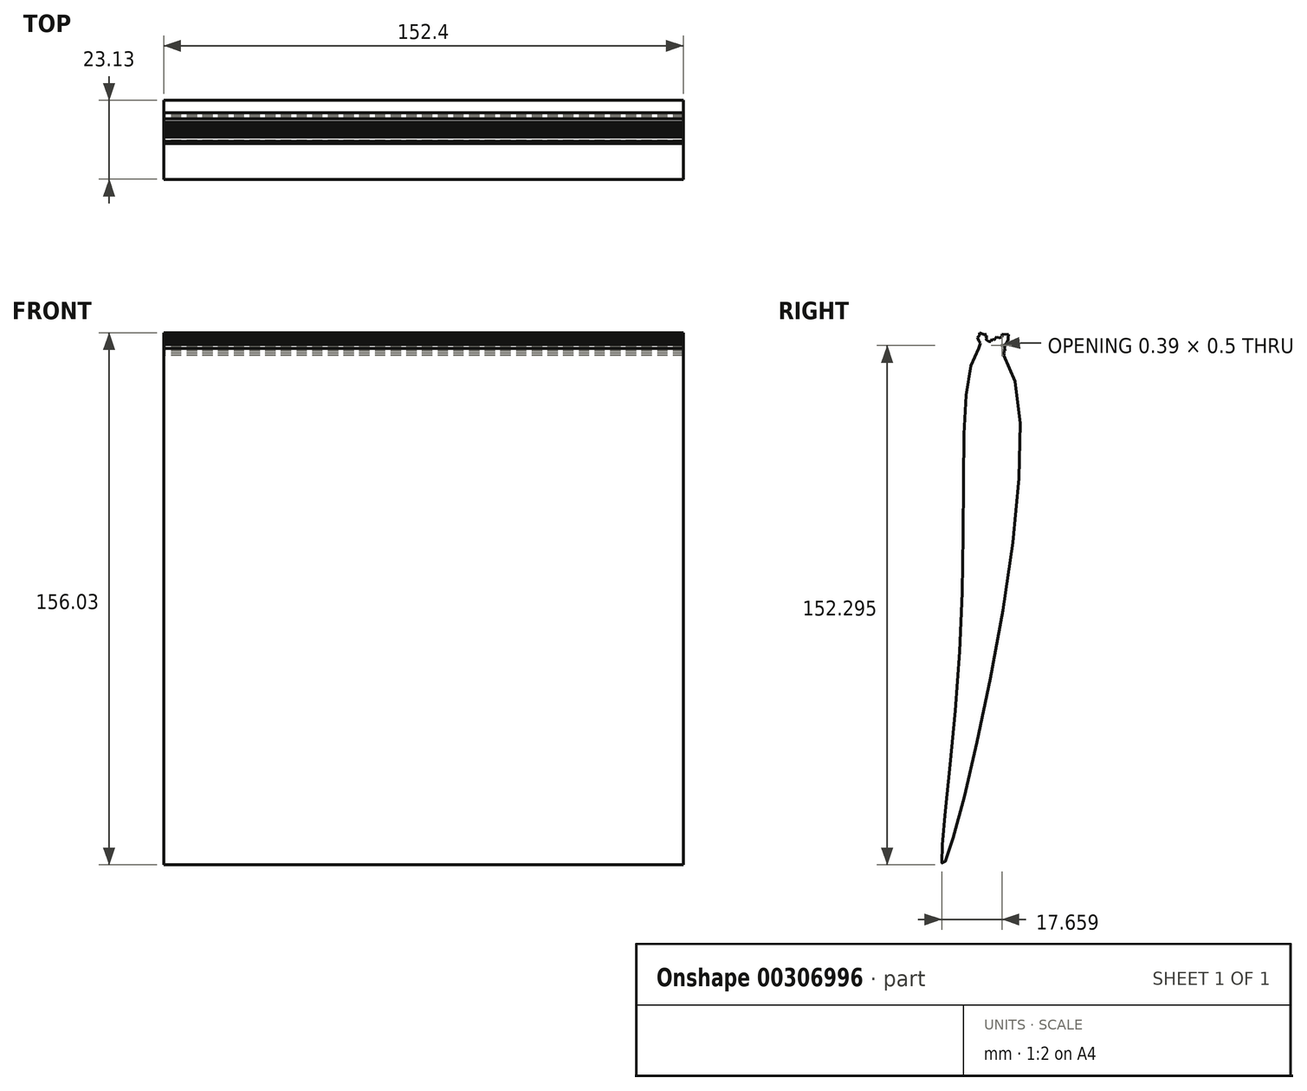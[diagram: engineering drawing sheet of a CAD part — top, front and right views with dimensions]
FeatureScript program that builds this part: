
annotation { "Feature Type Name" : "Feature", "Feature Type Description" : "" }
export const myFeature = defineFeature(function(context is Context, id is Id, definition is map)
    precondition{}
    {
        {
            var Q0;
            Q0=qCreatedBy(makeId("Right.planeOp"),FACE);
            var sketch = newSketch(context, id + "F0", { "sketchPlane" : qUnion([Q0])});
            skFitSpline(sketch, "E0", {"points": [v(8.56, 74.97) * mm, v(19.4, 61.14) * mm, v(-2.03, -76.46) * mm, v(2.7, -8.93) * mm, v(8.56, 74.97) * mm]});
            skLineSegment(sketch, "E1", {"start": v(12.68, 75.05) * mm, "end": v(15.09, 77.75) * mm});
            skLineSegment(sketch, "E2", {"start": v(15.09, 77.75) * mm, "end": v(16.1, 76.96) * mm});
            skLineSegment(sketch, "E3", {"start": v(16.1, 76.96) * mm, "end": v(13.9, 74.13) * mm});
            skLineSegment(sketch, "E4", {"start": v(13.9, 74.13) * mm, "end": v(12.68, 75.05) * mm});
            skLineSegment(sketch, "E5", {"start": v(15.09, 77.75) * mm, "end": v(15.68, 78.5) * mm});
            skPoint(sketch, "E5.endSnap0", {"position": v(15.6, 77.36) * mm});
            skLineSegment(sketch, "E6", {"start": v(15.68, 78.5) * mm, "end": v(16.65, 77.64) * mm});
            skLineSegment(sketch, "E7", {"start": v(16.65, 77.64) * mm, "end": v(16.1, 76.96) * mm});
            skLineSegment(sketch, "E8", {"start": v(10.23, 75.65) * mm, "end": v(9.38, 78.15) * mm});
            skLineSegment(sketch, "E9", {"start": v(9.38, 78.15) * mm, "end": v(8.15, 77.73) * mm});
            skLineSegment(sketch, "E10", {"start": v(8.15, 77.73) * mm, "end": v(9, 75.25) * mm});
            skLineSegment(sketch, "E11", {"start": v(9, 75.25) * mm, "end": v(10.23, 75.65) * mm});
            skLineSegment(sketch, "E12", {"start": v(14.51, 73.62) * mm, "end": v(14.61, 75.05) * mm});
            skLineSegment(sketch, "E13", {"start": v(14.61, 75.05) * mm, "end": v(15, 75.55) * mm});
            skLineSegment(sketch, "E14", {"start": v(15, 75.55) * mm, "end": v(14.99, 75.28) * mm});
            skPoint(sketch, "E14.endSnap0", {"position": v(14.8, 75.3) * mm});
            skLineSegment(sketch, "E15", {"start": v(14.99, 75.28) * mm, "end": v(14.61, 75.05) * mm});
            skLineSegment(sketch, "E16", {"start": v(14.56, 74.33) * mm, "end": v(15.2, 75.14) * mm});
            skLineSegment(sketch, "E17", {"start": v(15.2, 75.14) * mm, "end": v(15.24, 75.85) * mm});
            skLineSegment(sketch, "E18", {"start": v(15.24, 75.85) * mm, "end": v(15.69, 75.5) * mm});
            skLineSegment(sketch, "E19", {"start": v(15.69, 75.5) * mm, "end": v(15.2, 75.14) * mm});
            skLineSegment(sketch, "E20", {"start": v(15.8, 76.57) * mm, "end": v(16.65, 76.5) * mm});
            skLineSegment(sketch, "E21", {"start": v(16.65, 76.5) * mm, "end": v(16.1, 76.96) * mm});
            skLineSegment(sketch, "E22", {"start": v(16.65, 77.64) * mm, "end": v(16.68, 76.92) * mm});
            skLineSegment(sketch, "E23", {"start": v(16.68, 76.92) * mm, "end": v(16.05, 76.11) * mm});
            skLineSegment(sketch, "E24", {"start": v(16.05, 76.11) * mm, "end": v(15.24, 75.85) * mm});
            skLineSegment(sketch, "E25", {"start": v(16.05, 76.11) * mm, "end": v(16.03, 75.8) * mm});
            skLineSegment(sketch, "E26", {"start": v(16.03, 75.8) * mm, "end": v(15.69, 75.5) * mm});
            skLineSegment(sketch, "E27", {"start": v(16.68, 76.92) * mm, "end": v(16.1, 76.96) * mm});
            skLineSegment(sketch, "E28", {"start": v(15.69, 75.5) * mm, "end": v(15.62, 74.53) * mm});
            skLineSegment(sketch, "E29", {"start": v(15.62, 74.53) * mm, "end": v(14.56, 74.33) * mm});
            skLineSegment(sketch, "E30", {"start": v(16.65, 77.64) * mm, "end": v(16.7, 78.44) * mm});
            skLineSegment(sketch, "E31", {"start": v(16.7, 78.44) * mm, "end": v(16.31, 77.94) * mm});
            skLineSegment(sketch, "E32", {"start": v(16.31, 77.94) * mm, "end": v(16.7, 78.44) * mm});
            skLineSegment(sketch, "E33", {"start": v(16.7, 78.44) * mm, "end": v(15.68, 78.5) * mm});
            skLineSegment(sketch, "E34", {"start": v(15.68, 78.5) * mm, "end": v(14.86, 78.57) * mm});
            skLineSegment(sketch, "E35", {"start": v(14.86, 78.57) * mm, "end": v(14.8, 77.77) * mm});
            skLineSegment(sketch, "E36", {"start": v(14.8, 77.77) * mm, "end": v(13.84, 77.48) * mm});
            skLineSegment(sketch, "E37", {"start": v(13.84, 77.48) * mm, "end": v(13.33, 77.88) * mm});
            skLineSegment(sketch, "E38", {"start": v(13.33, 77.88) * mm, "end": v(13.25, 76.74) * mm});
            skLineSegment(sketch, "E39", {"start": v(13.25, 76.74) * mm, "end": v(13.22, 76.31) * mm});
            skLineSegment(sketch, "E40", {"start": v(13.22, 76.31) * mm, "end": v(12.5, 76.19) * mm});
            skLineSegment(sketch, "E41", {"start": v(12.5, 76.19) * mm, "end": v(12.43, 75.3) * mm});
            skLineSegment(sketch, "E42", {"start": v(12.43, 75.3) * mm, "end": v(12.68, 75.05) * mm});
            skLineSegment(sketch, "E43", {"start": v(13.33, 77.88) * mm, "end": v(12.49, 76.8) * mm});
            skLineSegment(sketch, "E44", {"start": v(12.49, 76.8) * mm, "end": v(11.9, 77.25) * mm});
            skLineSegment(sketch, "E45", {"start": v(11.9, 77.25) * mm, "end": v(11.6, 76.43) * mm});
            skLineSegment(sketch, "E46", {"start": v(11.6, 76.43) * mm, "end": v(10.9, 76.48) * mm});
            skLineSegment(sketch, "E47", {"start": v(10.9, 76.48) * mm, "end": v(10.4, 75.84) * mm});
            skLineSegment(sketch, "E48", {"start": v(10.9, 76.48) * mm, "end": v(10.28, 76.95) * mm});
            skLineSegment(sketch, "E49", {"start": v(10.28, 76.95) * mm, "end": v(9.96, 76.54) * mm});
            skLineSegment(sketch, "E50", {"start": v(9.96, 76.54) * mm, "end": v(10.02, 77.38) * mm});
            skLineSegment(sketch, "E51", {"start": v(10.02, 77.38) * mm, "end": v(9.51, 77.78) * mm});
            skLineSegment(sketch, "E52", {"start": v(9.51, 77.78) * mm, "end": v(9.38, 78.15) * mm});
            skLineSegment(sketch, "E53", {"start": v(10.02, 77.38) * mm, "end": v(10.07, 78.1) * mm});
            skLineSegment(sketch, "E54", {"start": v(10.07, 78.1) * mm, "end": v(9.51, 77.78) * mm});
            skLineSegment(sketch, "E55", {"start": v(10.07, 78.1) * mm, "end": v(10.58, 77.7) * mm});
            skLineSegment(sketch, "E56", {"start": v(10.58, 77.7) * mm, "end": v(10.02, 77.38) * mm});
            skLineSegment(sketch, "E57", {"start": v(10.07, 78.1) * mm, "end": v(9.8, 78.92) * mm});
            skLineSegment(sketch, "E58", {"start": v(9.8, 78.92) * mm, "end": v(9.38, 78.15) * mm});
            skLineSegment(sketch, "E59", {"start": v(9.38, 78.15) * mm, "end": v(8.8, 78.6) * mm});
            skPoint(sketch, "E59.endSnap0", {"position": v(8.76, 77.94) * mm});
            skLineSegment(sketch, "E60", {"start": v(8.8, 78.6) * mm, "end": v(8.15, 77.73) * mm});
            skLineSegment(sketch, "E61", {"start": v(8.15, 77.73) * mm, "end": v(8.24, 79.03) * mm});
            skLineSegment(sketch, "E62", {"start": v(8.24, 79.03) * mm, "end": v(9.59, 78.54) * mm});
            skLineSegment(sketch, "E63", {"start": v(9.59, 78.54) * mm, "end": v(9.8, 78.92) * mm});
            skLineSegment(sketch, "E64", {"start": v(8.18, 78.24) * mm, "end": v(7.64, 77.55) * mm});
            skLineSegment(sketch, "E65", {"start": v(7.64, 77.55) * mm, "end": v(8.65, 76.31) * mm});
            skLineSegment(sketch, "E66", {"start": v(8.65, 76.31) * mm, "end": v(7.97, 76.68) * mm});
            skLineSegment(sketch, "E67", {"start": v(7.97, 76.68) * mm, "end": v(7.82, 77.12) * mm});
            skLineSegment(sketch, "E68", {"start": v(7.82, 77.12) * mm, "end": v(7.64, 77.55) * mm});
            skLineSegment(sketch, "E69", {"start": v(9, 75.25) * mm, "end": v(8.56, 74.97) * mm});
            skLineSegment(sketch, "E70", {"start": v(8.56, 74.97) * mm, "end": v(8.34, 75.62) * mm});
            skLineSegment(sketch, "E71", {"start": v(8.34, 75.62) * mm, "end": v(8.72, 76.22) * mm});
            skLineSegment(sketch, "E72", {"start": v(8.72, 76.22) * mm, "end": v(7.97, 76.68) * mm});
            skLineSegment(sketch, "E73", {"start": v(7.97, 76.68) * mm, "end": v(8.53, 75.92) * mm});
            skLineSegment(sketch, "E74", {"start": v(15.62, 74.53) * mm, "end": v(15.75, 73.84) * mm});
            skLineSegment(sketch, "E75", {"start": v(15.75, 73.84) * mm, "end": v(15.24, 73.69) * mm});
            skLineSegment(sketch, "E76", {"start": v(15.24, 73.69) * mm, "end": v(15.43, 73.08) * mm});
            skLineSegment(sketch, "E77", {"start": v(15.43, 73.08) * mm, "end": v(15.38, 72.41) * mm});
            skLineSegment(sketch, "E78", {"start": v(15.38, 72.41) * mm, "end": v(14.51, 73.62) * mm});
            skLineSegment(sketch, "E79", {"start": v(8.34, 75.62) * mm, "end": v(8.02, 74.48) * mm});
            skLineSegment(sketch, "E80", {"start": v(8.02, 74.48) * mm, "end": v(8.56, 74.97) * mm});
            skLineSegment(sketch, "E81", {"start": v(10.02, 77.38) * mm, "end": v(10.28, 76.95) * mm});
            skLineSegment(sketch, "E82.0", {"start": v(8.34, 75.62) * mm, "end": v(15.2, 75.14) * mm, "construction": true});
            skLineSegment(sketch, "E83.0", {"start": v(7.82, 77.12) * mm, "end": v(16.65, 76.5) * mm, "construction": true});
            skLineSegment(sketch, "E84.0", {"start": v(7.97, 76.68) * mm, "end": v(10.9, 76.48) * mm, "construction": true});
            skLineSegment(sketch, "E85.0", {"start": v(8.65, 76.31) * mm, "end": v(16.03, 75.8) * mm, "construction": true});
            skLineSegment(sketch, "E86.0", {"start": v(7.64, 77.55) * mm, "end": v(16.68, 76.92) * mm, "construction": true});
            skLineSegment(sketch, "E87.0", {"start": v(8.24, 79.03) * mm, "end": v(16.7, 78.44) * mm, "construction": true});
            skLineSegment(sketch, "E88.0", {"start": v(8.18, 78.24) * mm, "end": v(16.65, 77.64) * mm, "construction": true});
            skLineSegment(sketch, "E89.0", {"start": v(9.51, 77.78) * mm, "end": v(15.6, 77.36) * mm, "construction": true});
            skLineSegment(sketch, "E90.0", {"start": v(14.8, 75.3) * mm, "end": v(14.99, 75.28) * mm, "construction": true});
            skLineSegment(sketch, "E91.0", {"start": v(12.49, 76.8) * mm, "end": v(13.25, 76.74) * mm, "construction": true});
            skLineSegment(sketch, "E92.0", {"start": v(13.22, 76.31) * mm, "end": v(16.05, 76.11) * mm, "construction": true});
            skLineSegment(sketch, "E93.0", {"start": v(8.65, 76.31) * mm, "end": v(8.8, 78.6) * mm, "construction": true});
            skLineSegment(sketch, "E94.0", {"start": v(16.05, 76.11) * mm, "end": v(16.1, 76.96) * mm, "construction": true});
            skLineSegment(sketch, "E95.0", {"start": v(8.15, 77.73) * mm, "end": v(8.18, 78.24) * mm, "construction": true});
            skLineSegment(sketch, "E96.0", {"start": v(15.6, 77.36) * mm, "end": v(15.68, 78.5) * mm, "construction": true});
            skLineSegment(sketch, "E97.0", {"start": v(14.56, 74.33) * mm, "end": v(14.86, 78.57) * mm, "construction": true});
            skLineSegment(sketch, "E98.0", {"start": v(16.65, 76.5) * mm, "end": v(16.68, 76.92) * mm, "construction": true});
            skSolve(sketch);
        }
        {
            var Q0;
            Q0=qSketchRegion(id+"F0",true);
            var Q1;
            Q1=makeQuery(id+"F0.imprint","IMPRINT",FACE,{"disambiguationData":[TD([[makeQuery(id+"F0.imprint","IMPRINT",EDGE,{"derivedFrom":sQuery(id+"F0.wireOp",EDGE,"E1")}),1.0]])]});
            var Q2;
            {var subQ3=sQuery(id+"F0.wireOp",EDGE,"E1");Q2=makeQuery(id+"F0.imprint","IMPRINT",FACE,{"disambiguationData":[TD([[makeQuery(id+"F0.imprint","IMPRINT",EDGE,{"derivedFrom":subQ3}),-1.0]])]});}
            var Q3;
            {var subQ0=sQuery(id+"F0.wireOp",EDGE,"E29");Q3=makeQuery(id+"F0.imprint","IMPRINT",FACE,{"disambiguationData":[TD([[makeQuery(id+"F0.imprint","IMPRINT",EDGE,{"derivedFrom":subQ0}),1.0]])]});}
            var Q4;
            {var subQ0=sQuery(id+"F0.wireOp",EDGE,"E78");var subQ1=sQuery(id+"F0.wireOp",EDGE,"E12");var subQ2=makeQuery(id+"F0.imprint","INTERSECT",VERTEX,{"derivedFrom":[subQ1,subQ0]});Q4=makeQuery(id+"F0.imprint","IMPRINT",FACE,{"disambiguationData":[TD([[makeQuery(id+"F0.imprint","IMPRINT",EDGE,{"disambiguationData":[TD([[subQ2,1.0]])],"derivedFrom":subQ0}),1.0]])]});}
            var Q5;
            {var subQ2=sQuery(id+"F0.wireOp",EDGE,"E8");Q5=makeQuery(id+"F0.imprint","IMPRINT",FACE,{"disambiguationData":[TD([[makeQuery(id+"F0.imprint","IMPRINT",EDGE,{"derivedFrom":subQ2}),-1.0]])]});}
            var Q6;
            {var subQ0=sQuery(id+"F0.wireOp",EDGE,"E11");Q6=makeQuery(id+"F0.imprint","IMPRINT",FACE,{"disambiguationData":[TD([[makeQuery(id+"F0.imprint","IMPRINT",EDGE,{"derivedFrom":subQ0}),1.0]])]});}
            var Q7;
            {var subQ0=sQuery(id+"F0.wireOp",EDGE,"E4");Q7=makeQuery(id+"F0.imprint","IMPRINT",FACE,{"disambiguationData":[TD([[makeQuery(id+"F0.imprint","IMPRINT",EDGE,{"derivedFrom":subQ0}),-1.0]])]});}
            var Q8;
            {var subQ0=sQuery(id+"F0.wireOp",EDGE,"E78");var subQ1=sQuery(id+"F0.wireOp",EDGE,"E0");var subQ3=makeQuery(id+"F0.imprint","INTERSECT",VERTEX,{"derivedFrom":[subQ1,subQ0]});Q8=makeQuery(id+"F0.imprint","IMPRINT",FACE,{"disambiguationData":[TD([[makeQuery(id+"F0.imprint","IMPRINT",EDGE,{"disambiguationData":[TD([[subQ3,-1.0]])],"derivedFrom":subQ1}),-1.0]])]});}
            var Q9;
            {var subQ6=sQuery(id+"F0.wireOp",EDGE,"E8");Q9=makeQuery(id+"F0.imprint","IMPRINT",FACE,{"disambiguationData":[TD([[makeQuery(id+"F0.imprint","IMPRINT",EDGE,{"derivedFrom":subQ6}),1.0]])]});}
            var Q10;
            Q10=makeQuery(id+"F0.imprint","IMPRINT",FACE,{"disambiguationData":[TD([[makeQuery(id+"F0.imprint","IMPRINT",EDGE,{"derivedFrom":sQuery(id+"F0.wireOp",EDGE,"E58")}),-1.0]])]});
            var Q11;
            {var subQ0=sQuery(id+"F0.wireOp",EDGE,"E69");Q11=makeQuery(id+"F0.imprint","IMPRINT",FACE,{"disambiguationData":[TD([[makeQuery(id+"F0.imprint","IMPRINT",EDGE,{"derivedFrom":subQ0}),-1.0]])]});}
            var Q12;
            {var subQ1=sQuery(id+"F0.wireOp",EDGE,"E70");Q12=makeQuery(id+"F0.imprint","IMPRINT",FACE,{"disambiguationData":[TD([[makeQuery(id+"F0.imprint","IMPRINT",EDGE,{"derivedFrom":subQ1}),1.0]])]});}
            var Q13;
            {var subQ0=sQuery(id+"F0.wireOp",EDGE,"E80");Q13=makeQuery(id+"F0.imprint","IMPRINT",FACE,{"disambiguationData":[TD([[makeQuery(id+"F0.imprint","IMPRINT",EDGE,{"derivedFrom":subQ0}),1.0]])]});}
            var Q14;
            {var subQ5=sQuery(id+"F0.wireOp",EDGE,"E64");Q14=makeQuery(id+"F0.imprint","IMPRINT",FACE,{"disambiguationData":[TD([[makeQuery(id+"F0.imprint","IMPRINT",EDGE,{"derivedFrom":subQ5}),1.0]])]});}
            var Q15;
            {var subQ1=sQuery(id+"F0.wireOp",EDGE,"E70");Q15=makeQuery(id+"F0.imprint","IMPRINT",FACE,{"disambiguationData":[TD([[makeQuery(id+"F0.imprint","IMPRINT",EDGE,{"derivedFrom":subQ1}),-1.0]])]});}
            var Q16;
            {var subQ0=sQuery(id+"F0.wireOp",EDGE,"E67");Q16=makeQuery(id+"F0.imprint","IMPRINT",FACE,{"disambiguationData":[TD([[makeQuery(id+"F0.imprint","IMPRINT",EDGE,{"derivedFrom":subQ0}),-1.0]])]});}
            var Q17;
            {var subQ0=sQuery(id+"F0.wireOp",EDGE,"E72");var subQ1=sQuery(id+"F0.wireOp",EDGE,"E10");var subQ2=makeQuery(id+"F0.imprint","INTERSECT",VERTEX,{"derivedFrom":[subQ1,subQ0]});Q17=makeQuery(id+"F0.imprint","IMPRINT",FACE,{"disambiguationData":[TD([[makeQuery(id+"F0.imprint","IMPRINT",EDGE,{"disambiguationData":[TD([[subQ2,-1.0]])],"derivedFrom":subQ1}),1.0]])]});}
            var Q18;
            Q18=makeQuery(id+"F0.imprint","IMPRINT",FACE,{"disambiguationData":[TD([[makeQuery(id+"F0.imprint","IMPRINT",EDGE,{"derivedFrom":sQuery(id+"F0.wireOp",EDGE,"E9")}),-1.0]])]});
            var Q19;
            Q19=makeQuery(id+"F0.imprint","IMPRINT",FACE,{"disambiguationData":[TD([[makeQuery(id+"F0.imprint","IMPRINT",EDGE,{"derivedFrom":sQuery(id+"F0.wireOp",EDGE,"E17")}),-1.0]])]});
            var Q20;
            {var subQ0=sQuery(id+"F0.wireOp",EDGE,"E65");var subQ1=sQuery(id+"F0.wireOp",EDGE,"E10");var subQ2=makeQuery(id+"F0.imprint","INTERSECT",VERTEX,{"derivedFrom":[subQ1,subQ0]});Q20=makeQuery(id+"F0.imprint","IMPRINT",FACE,{"disambiguationData":[TD([[makeQuery(id+"F0.imprint","IMPRINT",EDGE,{"disambiguationData":[TD([[subQ2,-1.0]])],"derivedFrom":subQ1}),1.0]])]});}
            var Q21;
            Q21=makeQuery(id+"F0.imprint","IMPRINT",FACE,{"disambiguationData":[TD([[makeQuery(id+"F0.imprint","IMPRINT",EDGE,{"derivedFrom":sQuery(id+"F0.wireOp",EDGE,"E18")}),1.0]])]});
            var Q22;
            Q22=makeQuery(id+"F0.imprint","IMPRINT",FACE,{"disambiguationData":[TD([[makeQuery(id+"F0.imprint","IMPRINT",EDGE,{"derivedFrom":sQuery(id+"F0.wireOp",EDGE,"E49")}),-1.0]])]});
            var Q23;
            {var subQ2=sQuery(id+"F0.wireOp",EDGE,"E32");Q23=makeQuery(id+"F0.imprint","IMPRINT",FACE,{"disambiguationData":[TD([[makeQuery(id+"F0.imprint","IMPRINT",EDGE,{"derivedFrom":subQ2}),1.0]])]});}
            var Q24;
            {var subQ0=sQuery(id+"F0.wireOp",EDGE,"E66");var subQ1=sQuery(id+"F0.wireOp",EDGE,"E10");var subQ2=makeQuery(id+"F0.imprint","INTERSECT",VERTEX,{"derivedFrom":[subQ1,subQ0]});Q24=makeQuery(id+"F0.imprint","IMPRINT",FACE,{"disambiguationData":[TD([[makeQuery(id+"F0.imprint","IMPRINT",EDGE,{"disambiguationData":[TD([[subQ2,-1.0]])],"derivedFrom":subQ1}),-1.0]])]});}
            var Q25;
            Q25=makeQuery(id+"F0.imprint","IMPRINT",FACE,{"disambiguationData":[TD([[makeQuery(id+"F0.imprint","IMPRINT",EDGE,{"derivedFrom":sQuery(id+"F0.wireOp",EDGE,"E2")}),1.0]])]});
            var Q26;
            {var subQ5=sQuery(id+"F0.wireOp",EDGE,"E73");Q26=makeQuery(id+"F0.imprint","IMPRINT",FACE,{"disambiguationData":[TD([[makeQuery(id+"F0.imprint","IMPRINT",EDGE,{"derivedFrom":subQ5}),1.0]])]});}
            var Q27;
            {var subQ1=sQuery(id+"F0.wireOp",EDGE,"E14");Q27=makeQuery(id+"F0.imprint","IMPRINT",FACE,{"disambiguationData":[TD([[makeQuery(id+"F0.imprint","IMPRINT",EDGE,{"derivedFrom":subQ1}),1.0]])]});}
            var Q28;
            Q28=makeQuery(id+"F0.imprint","IMPRINT",FACE,{"disambiguationData":[TD([[makeQuery(id+"F0.imprint","IMPRINT",EDGE,{"derivedFrom":sQuery(id+"F0.wireOp",EDGE,"E16")}),-1.0]])]});
            var Q29;
            {var subQ0=sQuery(id+"F0.wireOp",EDGE,"E24");Q29=makeQuery(id+"F0.imprint","IMPRINT",FACE,{"disambiguationData":[TD([[makeQuery(id+"F0.imprint","IMPRINT",EDGE,{"derivedFrom":subQ0}),-1.0]])]});}
            var Q30;
            Q30=makeQuery(id+"F0.imprint","IMPRINT",FACE,{"disambiguationData":[TD([[makeQuery(id+"F0.imprint","IMPRINT",EDGE,{"derivedFrom":sQuery(id+"F0.wireOp",EDGE,"E13")}),-1.0]])]});
            var Q31;
            {var subQ0=sQuery(id+"F0.wireOp",EDGE,"E21");var subQ1=sQuery(id+"F0.wireOp",EDGE,"E20");var subQ2=makeQuery(id+"F0.imprint","INTERSECT",VERTEX,{"derivedFrom":[subQ1,subQ0]});Q31=makeQuery(id+"F0.imprint","IMPRINT",FACE,{"disambiguationData":[TD([[makeQuery(id+"F0.imprint","IMPRINT",EDGE,{"disambiguationData":[TD([[subQ2,1.0]])],"derivedFrom":subQ1}),1.0]])]});}
            var Q32;
            Q32=makeQuery(id+"F0.imprint","IMPRINT",FACE,{"disambiguationData":[TD([[makeQuery(id+"F0.imprint","IMPRINT",EDGE,{"derivedFrom":sQuery(id+"F0.wireOp",EDGE,"E53")}),-1.0]])]});
            var Q33;
            {var subQ0=sQuery(id+"F0.wireOp",EDGE,"E30");Q33=makeQuery(id+"F0.imprint","IMPRINT",FACE,{"disambiguationData":[TD([[makeQuery(id+"F0.imprint","IMPRINT",EDGE,{"derivedFrom":subQ0}),1.0]])]});}
            var Q34;
            Q34=makeQuery(id+"F0.imprint","IMPRINT",FACE,{"disambiguationData":[TD([[makeQuery(id+"F0.imprint","IMPRINT",EDGE,{"derivedFrom":sQuery(id+"F0.wireOp",EDGE,"E7")}),1.0]])]});
            var Q35;
            Q35=makeQuery(id+"F0.imprint","IMPRINT",FACE,{"disambiguationData":[TD([[makeQuery(id+"F0.imprint","IMPRINT",EDGE,{"derivedFrom":sQuery(id+"F0.wireOp",EDGE,"E51")}),-1.0]])]});
            var Q36;
            Q36=makeQuery(id+"F0.imprint","IMPRINT",FACE,{"disambiguationData":[TD([[makeQuery(id+"F0.imprint","IMPRINT",EDGE,{"derivedFrom":sQuery(id+"F0.wireOp",EDGE,"E52")}),-1.0]])]});
            var Q37;
            {var subQ1=sQuery(id+"F0.wireOp",EDGE,"E3");var subQ3=sQuery(id+"F0.wireOp",EDGE,"E20");var subQ4=makeQuery(id+"F0.imprint","INTERSECT",VERTEX,{"derivedFrom":[subQ1,subQ3]});Q37=makeQuery(id+"F0.imprint","IMPRINT",FACE,{"disambiguationData":[TD([[makeQuery(id+"F0.imprint","IMPRINT",EDGE,{"disambiguationData":[TD([[subQ4,-1.0]])],"derivedFrom":subQ3}),1.0]])]});}
            var Q38;
            {var subQ0=sQuery(id+"F0.wireOp",EDGE,"E27");Q38=makeQuery(id+"F0.imprint","IMPRINT",FACE,{"disambiguationData":[TD([[makeQuery(id+"F0.imprint","IMPRINT",EDGE,{"derivedFrom":subQ0}),1.0]])]});}
            var Q39;
            {var subQ4=sQuery(id+"F0.wireOp",EDGE,"E4");Q39=makeQuery(id+"F0.imprint","IMPRINT",FACE,{"disambiguationData":[TD([[makeQuery(id+"F0.imprint","IMPRINT",EDGE,{"derivedFrom":subQ4}),1.0]])]});}
            extrude(context, id + "F1", {"entities" : qUnion([Q0, Q1, Q2, Q3, Q4, Q5, Q6, Q7, Q8, Q9, Q10, Q11, Q12, Q13, Q14, Q15, Q16, Q17, Q18, Q19, Q20, Q21, Q22, Q23, Q24, Q25, Q26, Q27, Q28, Q29, Q30, Q31, Q32, Q33, Q34, Q35, Q36, Q37, Q38, Q39]), "depth" : 76.2 * mm, "hasSecondDirection" : true, "secondDirectionOppositeDirection" : true, "secondDirectionDepth" : 76.2 * mm});
        }
    });
